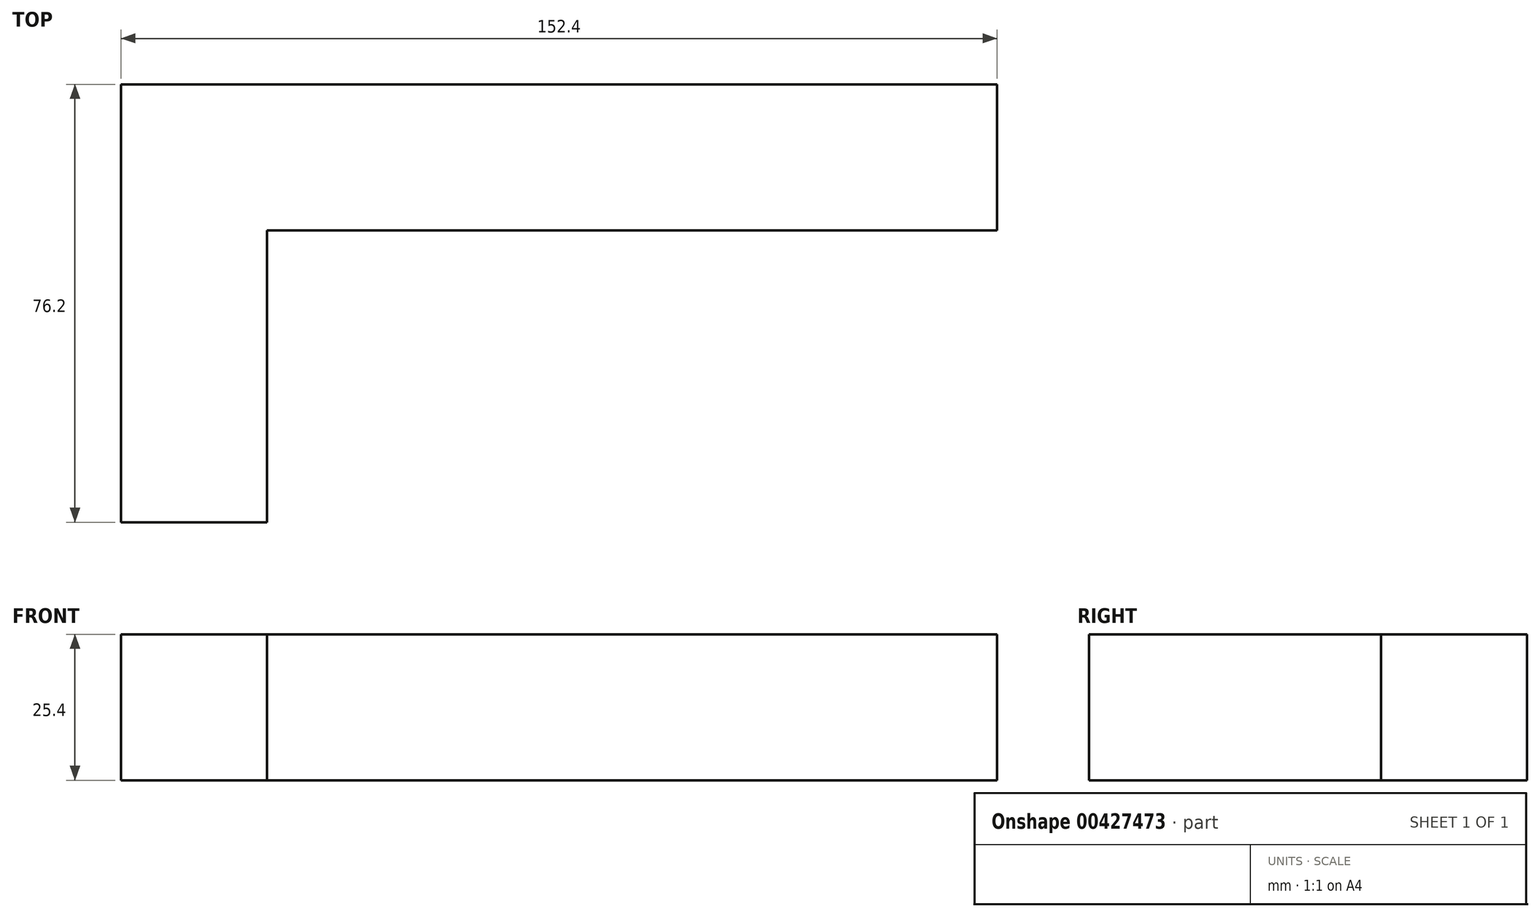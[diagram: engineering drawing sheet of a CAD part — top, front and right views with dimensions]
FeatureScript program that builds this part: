
annotation { "Feature Type Name" : "Feature", "Feature Type Description" : "" }
export const myFeature = defineFeature(function(context is Context, id is Id, definition is map)
    precondition{}
    {
        {
            var Q0;
            Q0=qCreatedBy(makeId("Top.planeOp"),FACE);
            var sketch = newSketch(context, id + "F0", { "sketchPlane" : qUnion([Q0])});
            skLineSegment(sketch, "E0", {"start": v(0, 0) * mm, "end": v(0, -76.2) * mm});
            skLineSegment(sketch, "E1", {"start": v(0, -76.2) * mm, "end": v(25.4, -76.2) * mm});
            skLineSegment(sketch, "E2", {"start": v(25.4, -76.2) * mm, "end": v(25.4, -25.4) * mm});
            skLineSegment(sketch, "E3", {"start": v(25.4, -25.4) * mm, "end": v(152.4, -25.4) * mm});
            skLineSegment(sketch, "E4", {"start": v(152.4, -25.4) * mm, "end": v(152.4, 0) * mm});
            skLineSegment(sketch, "E5", {"start": v(152.4, 0) * mm, "end": v(0, 0) * mm});
            skSolve(sketch);
        }
        {
            var Q0;
            Q0 = qSketchRegion(id + "F0", true);
            extrude(context, id + "F1", {"entities" : qUnion([Q0]), "depth" : 25.4 * mm});
        }
    });
